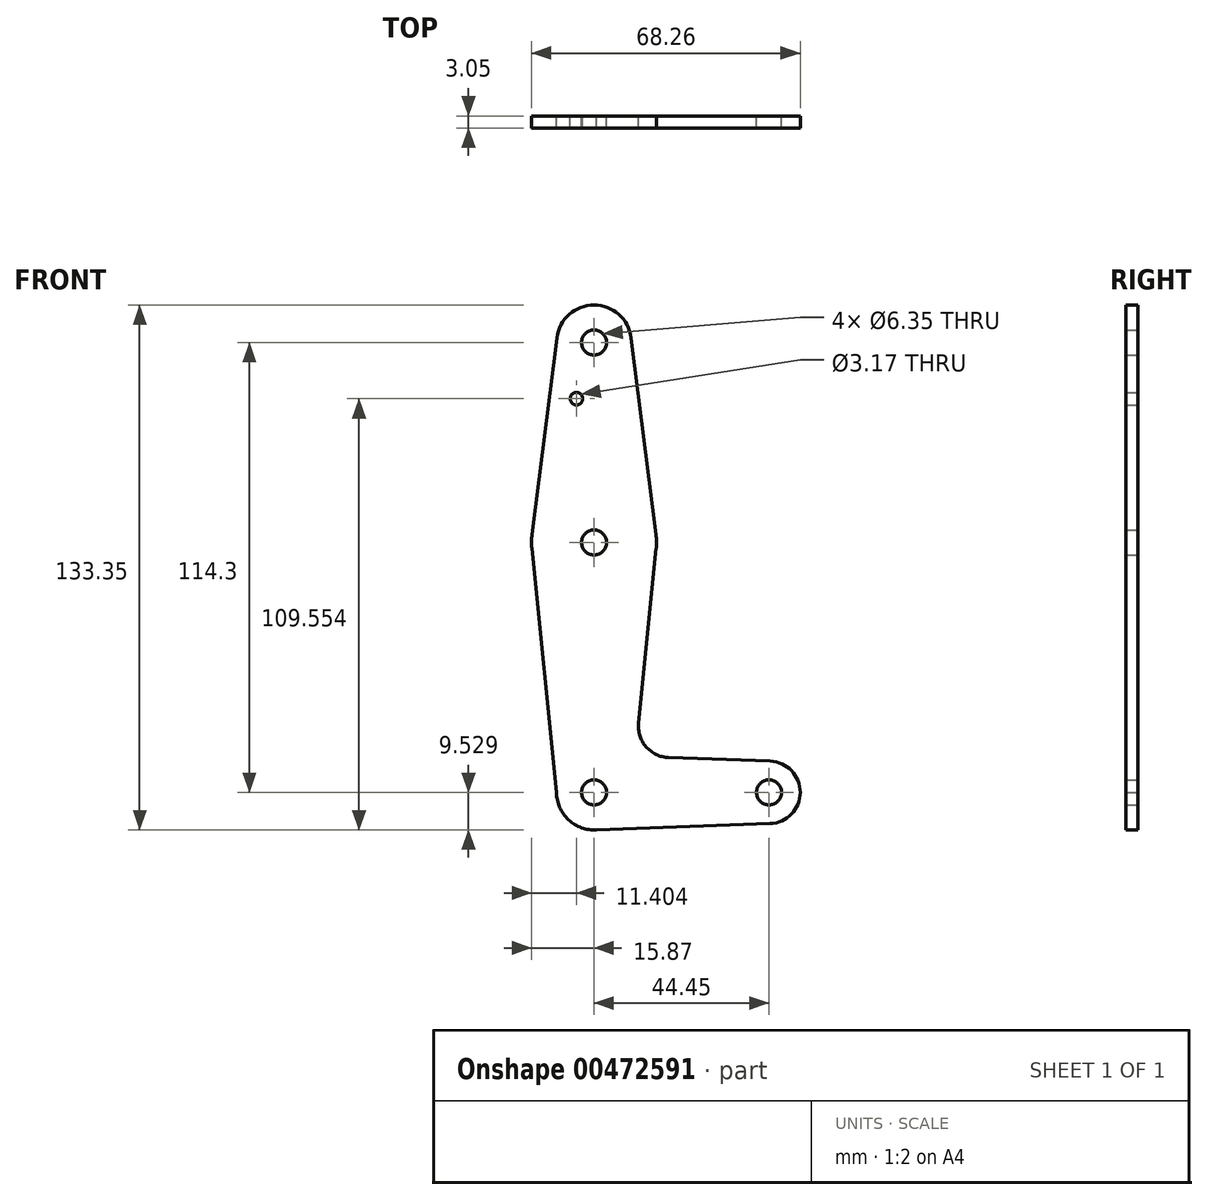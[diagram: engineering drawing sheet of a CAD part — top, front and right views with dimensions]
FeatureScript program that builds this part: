
annotation { "Feature Type Name" : "Feature", "Feature Type Description" : "" }
export const myFeature = defineFeature(function(context is Context, id is Id, definition is map)
    precondition{}
    {
        {
            var Q0;
            Q0=qCreatedBy(makeId("Front.planeOp"),FACE);
            var sketch = newSketch(context, id + "F0", { "sketchPlane" : qUnion([Q0])});
            skCircle(sketch, "E0", {"center": v(0, 32.38) * mm, "radius": 15.88 * mm});
            skCircle(sketch, "E1", {"center": v(0, -31.12) * mm, "radius": 9.53 * mm});
            skLineSegment(sketch, "E2", {"start": v(-9.52, -31.12) * mm, "end": v(-15.8, 30.78) * mm});
            skLineSegment(sketch, "E3", {"start": v(0, -31.12) * mm, "end": v(0, 83.18) * mm, "construction": true});
            skLineSegment(sketch, "E4", {"start": v(0, -31.12) * mm, "end": v(44.45, -31.12) * mm, "construction": true});
            skCircle(sketch, "E5", {"center": v(0, 83.18) * mm, "radius": 9.53 * mm});
            skCircle(sketch, "E6", {"center": v(44.45, -31.12) * mm, "radius": 7.94 * mm});
            skLineSegment(sketch, "E7", {"start": v(9.45, 84.37) * mm, "end": v(15.75, 34.36) * mm});
            skLineSegment(sketch, "E8", {"start": v(-9.45, 84.37) * mm, "end": v(-15.75, 34.36) * mm});
            skLineSegment(sketch, "E9", {"start": v(18.93, -22.27) * mm, "end": v(44.73, -23.19) * mm});
            skLineSegment(sketch, "E10", {"start": v(0, -40.65) * mm, "end": v(44.73, -39.05) * mm});
            skLineSegment(sketch, "E11", {"start": v(11.3, -13.52) * mm, "end": v(15.8, 30.78) * mm});
            skCircle(sketch, "E12", {"center": v(0, 83.18) * mm, "radius": 3.18 * mm});
            skCircle(sketch, "E13", {"center": v(0, 32.38) * mm, "radius": 3.18 * mm});
            skCircle(sketch, "E14", {"center": v(0, -31.12) * mm, "radius": 3.18 * mm});
            skCircle(sketch, "E15", {"center": v(44.45, -31.12) * mm, "radius": 3.18 * mm});
            skArc(sketch, "E16.filletArc", {"start": v(11.3, -13.52) * mm, "mid": v(13.22, -19.55) * mm, "end": v(18.93, -22.27) * mm});
            skCircle(sketch, "E17", {"center": v(-4.47, 68.9) * mm, "radius": 1.59 * mm});
            skSolve(sketch);
        }
        {
            var Q0;
            Q0 = qSketchRegion(id + "F0", true);
            extrude(context, id + "F1", {"entities" : qUnion([Q0]), "depth" : 3.05 * mm});
        }
    });
